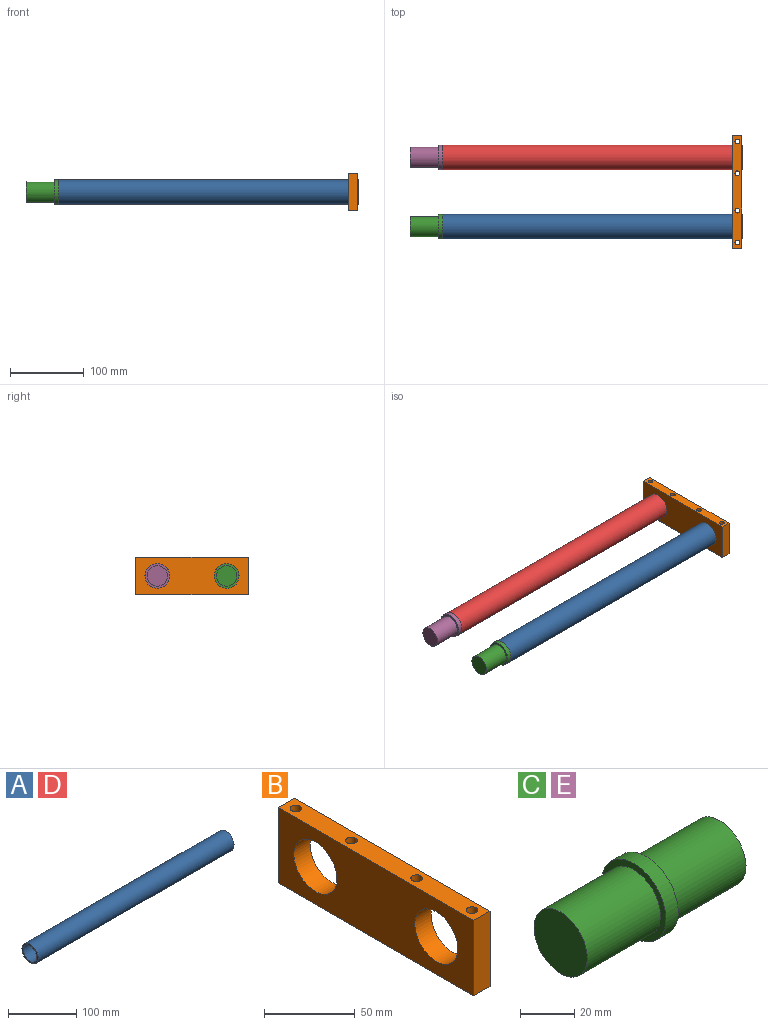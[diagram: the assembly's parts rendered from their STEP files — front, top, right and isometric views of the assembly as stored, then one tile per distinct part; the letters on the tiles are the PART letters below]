
ASSEMBLY  parts=5 mates=2
PART A: 4 faces, bbox 406.4x33.4x33.4 mm
  f0: cylinder r=13.93mm len=406.4mm, axis (1,0,0), area 35574.9mm2, adj f1,f2
  f1: plane 33.4x33.4mm, normal (-1,0,0), area 266.4mm2, adj f0,f3
  f2: plane 33.4x33.4mm, normal (1,0,0), area 266.4mm2, adj f0,f3
  f3: cylinder r=16.7mm len=406.4mm, axis (1,0,0), area 42644.5mm2, adj f1,f2
PART B: 12 faces, bbox 12.7x152.4x50.8 mm
  f0: plane 152.4x12.7mm, normal (0,0,1), area 1808.8mm2, adj f2,f3,f6,f7,f8,f9,f10,f11
  f1: plane 152.4x12.7mm, normal (0,0,-1), area 1808.8mm2, adj f2,f3,f6,f7,f8,f9,f10,f11
  f2: plane 50.8x12.7mm, normal (0,1,0), area 645.2mm2, adj f0,f1,f6,f7
  f3: plane 50.8x12.7mm, normal (0,-1,0), area 645.2mm2, adj f0,f1,f6,f7
  f4: cylinder r=16.76mm len=33.53mm, axis (1,0,0), area 1337.7mm2, adj f6,f7
  f5: cylinder r=16.76mm len=33.53mm, axis (1,0,0), area 1337.7mm2, adj f6,f7
  f6: plane 152.4x50.8mm, normal (-1,0,0), area 5976.1mm2, adj f0,f1,f2,f3,f4,f5
  f7: plane 152.4x50.8mm, normal (1,0,0), area 5976.1mm2, adj f0,f1,f2,f3,f4,f5
  f8: cylinder r=3.17mm len=50.8mm, axis (0,0,1), area 1013.4mm2, adj f0,f1
  f9: cylinder r=3.17mm len=50.8mm, axis (0,0,1), area 1013.4mm2, adj f0,f1
  f10: cylinder r=3.17mm len=50.8mm, axis (0,0,1), area 1013.4mm2, adj f0,f1
  f11: cylinder r=3.17mm len=50.8mm, axis (0,0,1), area 1013.4mm2, adj f0,f1
PART C: 7 faces, bbox 82.6x33.4x33.4 mm
  f0: cylinder r=16.7mm len=33.4mm, axis (-1,0,0), area 666.3mm2, adj f1,f2
  f1: plane 33.4x33.4mm, normal (1,0,0), area 274.2mm2, adj f0,f3
  f2: plane 33.4x33.4mm, normal (-1,0,0), area 274.2mm2, adj f0,f5
  f3: cylinder r=13.84mm len=38.1mm, axis (-1,0,0), area 3313.9mm2, adj f1,f4
  f4: plane 27.69x27.69mm, normal (1,0,0), area 602mm2, adj f3
  f5: cylinder r=13.84mm len=38.1mm, axis (1,0,0), area 3313.9mm2, adj f2,f6
  f6: plane 27.69x27.69mm, normal (-1,0,0), area 602mm2, adj f5
PART D: same geometry as A
PART E: same geometry as C
PLACE A t=(-1.14,192.7,14.22)mm
PLACE B t=(405.26,239.79,14.22)mm
PLACE C t=(-4.31,192.7,14.22)mm
PLACE D t=(-1.14,286.88,14.22)mm
PLACE E t=(-4.31,286.88,14.22)mm
MATE fastened A.f0 <-> C.f3  axis (-1,0,0) through (-1.14,192.7,14.22)mm
MATE fastened A.f0 <-> B.f4  axis (1,0,0) through (405.26,192.7,14.22)mm
